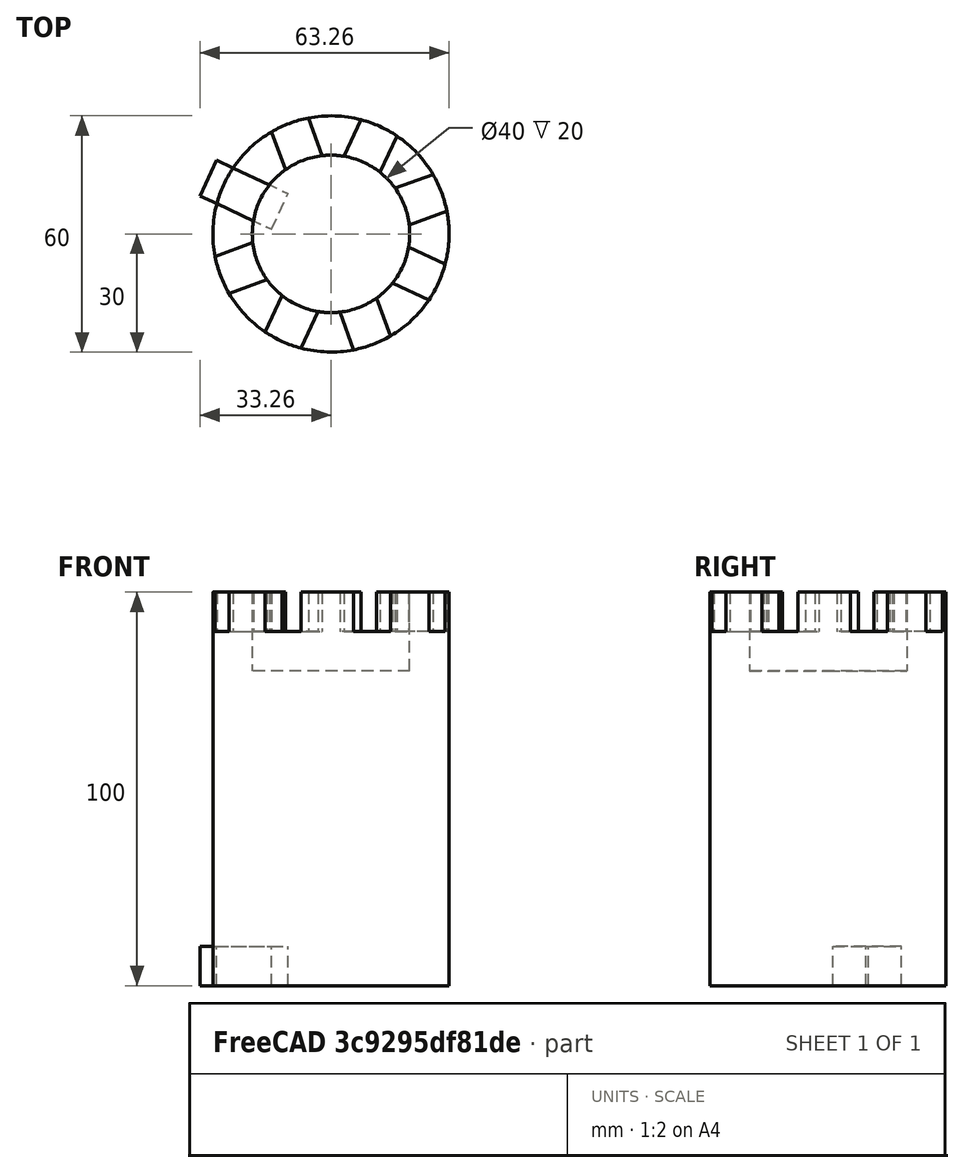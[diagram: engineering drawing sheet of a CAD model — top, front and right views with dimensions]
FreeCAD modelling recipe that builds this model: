
FCSTD DOCUMENT  (FreeCAD 1.0R39319 (Git))
Label: ojt1_t11r03_tower
License: All rights reserved
LicenseURL: https://en.wikipedia.org/wiki/All_rights_reserved
objects: Part::Cylinder×2, Part::Cut×2, Part::Box×1, Part::FeaturePython×1
note: 5 computed .brp shape members not serialized (recipe doc carries the construction recipe); baked Part::Feature solids carry a one-line shape summary decoded from their .brp

FEATURE [Part::Box] Box  label="Cub"
  AttacherType = Attacher::AttachEngine3D
  Height = 10
  Length = 20
  Placement = pos=(-33.26,9.63,0) rot=(0,0,-1;0.436332rad)
  Width = 10
FEATURE [Part::FeaturePython] Array  # Draft array (typed FeaturePython)
  AlwaysSyncPlacement = false
  Angle = 360
  ArrayType = 1
  Axis = (0,0,1)
  Base = -> Box
  Center = (0,0,0)
  Count = 8
  ExpandArray = false
  Fuse = false
  IntervalAxis = (0,0,0)
  IntervalX = (100,0,0)
  IntervalY = (0,100,0)
  IntervalZ = (0,0,100)
  NumberCircles = 3
  NumberPolar = 8
  NumberX = 2
  NumberY = 2
  NumberZ = 1
  Placement = pos=(0,0,90) rot=(0,0,1;0rad)
  PlacementList = 8 placements: [(-33.26,9.63,0),(-30.3278,-16.7089,0),(-9.63,-33.26,0),(16.7089,-30.3278,0),(33.26,-9.63,0),(30.3278,16.7089,0),(9.63,33.26,0),(-16.7089,30.3278,0)]
  RadialDistance = 50
  ScaleList = (8) [(1,1,1),(1,1,1),(1,1,1),(1,1,1),(1,1,1),(1,1,1),(1,1,1),(1,1,1)]
  Symmetry = 1
  TangentialDistance = 25
FEATURE [Part::Cylinder] Cylinder  label="base"
  Angle = 360
  AttacherType = Attacher::AttachEngine3D
  FirstAngle = 0
  Height = 100
  Radius = 30
  SecondAngle = 0
FEATURE [Part::Cylinder] Cylinder001  label="resta"
  Angle = 360
  AttacherType = Attacher::AttachEngine3D
  FirstAngle = 0
  Height = 20
  Placement = pos=(0,0,80) rot=(0,0,1;0rad)
  Radius = 20
  SecondAngle = 0
FEATURE [Part::Cut] Cut
  Base = -> Cylinder
  Tool = -> Cylinder001
FEATURE [Part::Cut] Cut001
  Base = -> Cut
  Tool = -> Array
